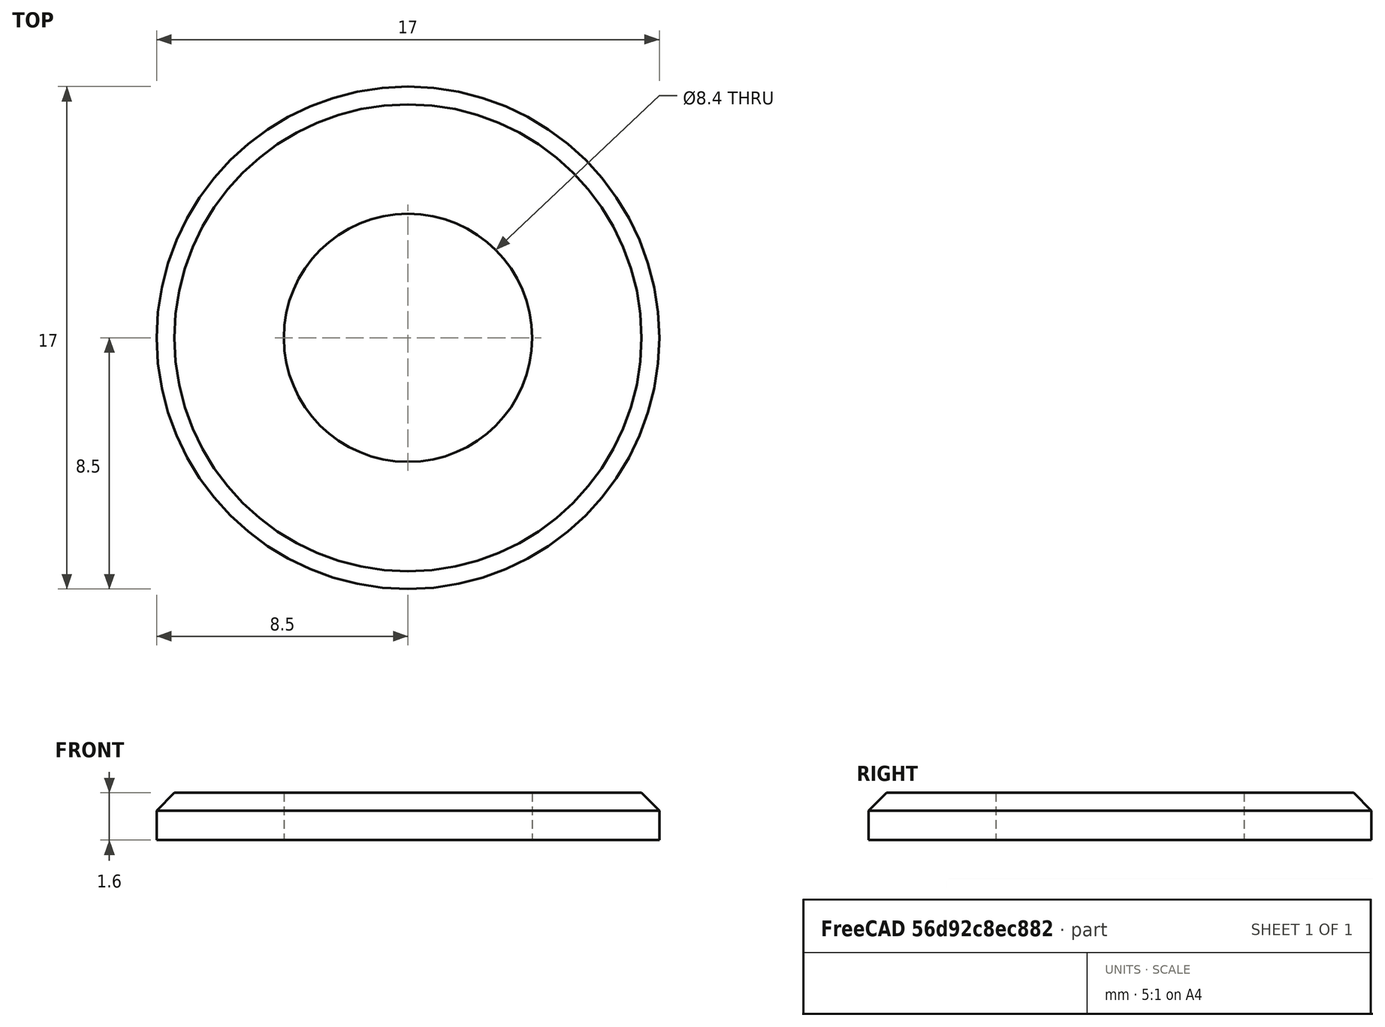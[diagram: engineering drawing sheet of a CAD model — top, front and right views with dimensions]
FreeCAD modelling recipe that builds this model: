
FCSTD DOCUMENT  (FreeCAD 0.15R4651 (Git))
Label: Scheibe_DIN125-B 8,4
License: CC-BY 3.0
LicenseURL: http://creativecommons.org/licenses/by/3.0/
objects: Sketcher::SketchObject×1, PartDesign::Revolution×1
note: 3 computed .brp shape members not serialized (recipe doc carries the construction recipe); baked Part::Feature solids carry a one-line shape summary decoded from their .brp

FEATURE [Sketcher::SketchObject] Sketch
  Placement = pos=(0,0,0) rot=(0.57735,0.57735,0.57735;2.0944rad)
  sketch-geometry (5):
    g0: LineSegment StartX=4.2 StartY=0 StartZ=0 EndX=8.5 EndY=0 EndZ=0
    g1: LineSegment StartX=8.5 StartY=0 StartZ=0 EndX=8.5 EndY=1 EndZ=0
    g2: LineSegment StartX=7.9 StartY=1.6 StartZ=0 EndX=4.2 EndY=1.6 EndZ=0
    g3: LineSegment StartX=4.2 StartY=1.6 StartZ=0 EndX=4.2 EndY=0 EndZ=0
    g4: LineSegment StartX=7.9 StartY=1.6 StartZ=0 EndX=8.5 EndY=1 EndZ=0
  constraints (15):
    c: Coincident(g0,g1)
    c: Coincident(g2,g3)
    c: Coincident(g3,g0)
    c: Horizontal(g0)
    c: Horizontal(g2)
    c: Vertical(g1)
    c: Vertical(g3)
    c: PointOnObject(g0,g-1)
    c: DistanceX(g-1,g2) = 4.2
    c: Coincident(g1,g4)
    c: Coincident(g2,g4)
    c: DistanceY(g3) = -1.6
    c: DistanceX(g-1,g1) = 8.5
    c: DistanceX(g4) = 0.6
    c: DistanceY(g4) = -0.6
FEATURE [PartDesign::Revolution] Revolution  label="Scheibe DIN 125 - B 8,4 #"
  Angle = 360
  Axis = (0,0,1)
  Base = (0,0,0)
  Placement = pos=(0,0,0) rot=(0.57735,0.57735,0.57735;2.0944rad)
  ReferenceAxis = -> Sketch [V_Axis]
  Reversed = true
  Sketch = -> Sketch
